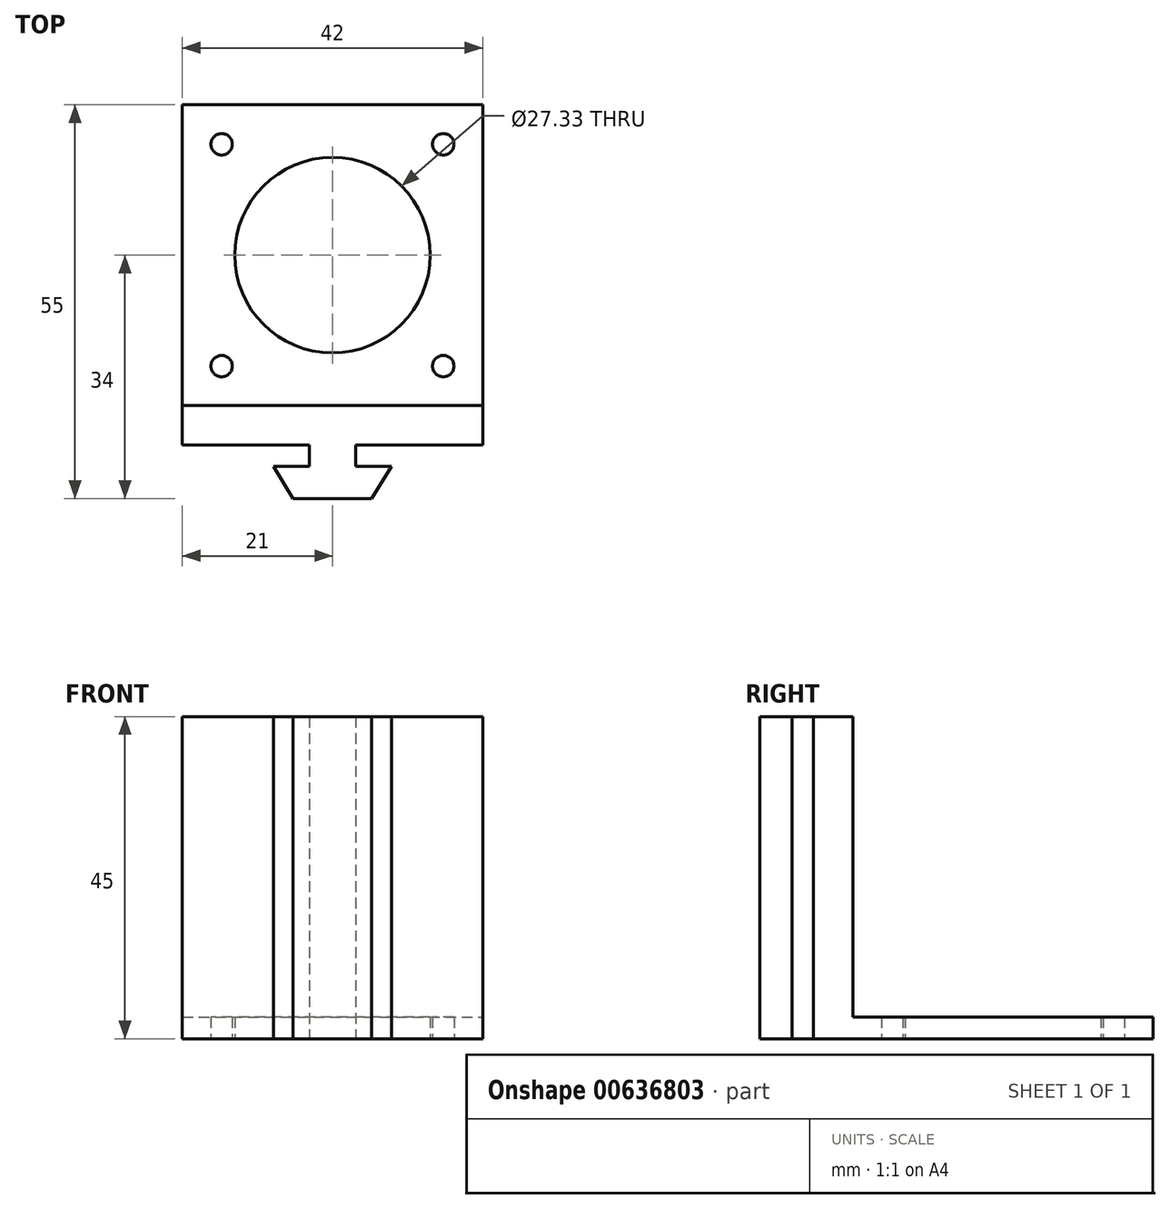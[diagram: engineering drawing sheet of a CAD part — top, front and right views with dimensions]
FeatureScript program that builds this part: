
annotation { "Feature Type Name" : "Feature", "Feature Type Description" : "" }
export const myFeature = defineFeature(function(context is Context, id is Id, definition is map)
    precondition{}
    {
        {
            var Q0;
            Q0=qCreatedBy(makeId("Top.planeOp"),FACE);
            var sketch = newSketch(context, id + "F0", { "sketchPlane" : qUnion([Q0])});
            skPoint(sketch, "E0.middle", {"position": v(0, 0) * mm});
            skLineSegment(sketch, "E1.bottom", {"start": v(-21, 21) * mm, "end": v(21, 21) * mm});
            skLineSegment(sketch, "E1.top", {"start": v(-21, -21) * mm, "end": v(21, -21) * mm});
            skLineSegment(sketch, "E1.left", {"start": v(-21, 21) * mm, "end": v(-21, -21) * mm});
            skLineSegment(sketch, "E1.right", {"start": v(21, 21) * mm, "end": v(21, -21) * mm});
            skLineSegment(sketch, "E2.bottom", {"start": v(15.5, -15.5) * mm, "end": v(-15.5, -15.5) * mm, "construction": true});
            skLineSegment(sketch, "E2.top", {"start": v(15.5, 15.5) * mm, "end": v(-15.5, 15.5) * mm, "construction": true});
            skLineSegment(sketch, "E2.left", {"start": v(15.5, -15.5) * mm, "end": v(15.5, 15.5) * mm, "construction": true});
            skLineSegment(sketch, "E2.right", {"start": v(-15.5, -15.5) * mm, "end": v(-15.5, 15.5) * mm, "construction": true});
            skCircle(sketch, "E3", {"center": v(-15.5, 15.5) * mm, "radius": 1.5 * mm});
            skCircle(sketch, "E4", {"center": v(15.5, 15.5) * mm, "radius": 1.5 * mm});
            skCircle(sketch, "E5", {"center": v(-15.5, -15.5) * mm, "radius": 1.5 * mm});
            skCircle(sketch, "E6", {"center": v(15.5, -15.5) * mm, "radius": 1.5 * mm});
            skLineSegment(sketch, "E7", {"start": v(0, -21) * mm, "end": v(3.25, -21) * mm});
            skLineSegment(sketch, "E8", {"start": v(3.25, -21) * mm, "end": v(3.25, -29.5) * mm});
            skLineSegment(sketch, "E9", {"start": v(3.25, -29.5) * mm, "end": v(8.25, -29.5) * mm});
            skLineSegment(sketch, "E10", {"start": v(0, -21) * mm, "end": v(0, -34) * mm});
            skLineSegment(sketch, "E11", {"start": v(0, -34) * mm, "end": v(5.5, -34) * mm});
            skLineSegment(sketch, "E12", {"start": v(5.5, -34) * mm, "end": v(8.25, -29.5) * mm});
            skLineSegment(sketch, "E13.MirrorCS", {"start": v(0, -34) * mm, "end": v(-5.5, -34) * mm});
            skLineSegment(sketch, "E14.MirrorCS", {"start": v(-5.5, -34) * mm, "end": v(-8.25, -29.5) * mm});
            skLineSegment(sketch, "E15.MirrorCS", {"start": v(-3.25, -29.5) * mm, "end": v(-8.25, -29.5) * mm});
            skLineSegment(sketch, "E16.MirrorCS", {"start": v(0, -21) * mm, "end": v(-3.25, -21) * mm});
            skLineSegment(sketch, "E17.MirrorCS", {"start": v(-3.25, -21) * mm, "end": v(-3.25, -26.5) * mm});
            skLineSegment(sketch, "E18.top", {"start": v(-21, -26.5) * mm, "end": v(21, -26.5) * mm});
            skLineSegment(sketch, "E18.left", {"start": v(-21, -21) * mm, "end": v(-21, -26.5) * mm});
            skLineSegment(sketch, "E18.right", {"start": v(21, -21) * mm, "end": v(21, -26.5) * mm});
            skCircle(sketch, "E19", {"center": v(0, 0) * mm, "radius": 13.67 * mm});
            skLineSegment(sketch, "E20", {"start": v(-3.25, -26.5) * mm, "end": v(-3.25, -29.5) * mm});
            skSolve(sketch);
        }
        {
            var Q0;
            Q0=makeQuery(id+"F0.imprint","IMPRINT",FACE,{"disambiguationData":[TD([[makeQuery(id+"F0.imprint","IMPRINT",EDGE,{"derivedFrom":sQuery(id+"F0.wireOp",EDGE,"E1.bottom")}),-1.0]])]});
            extrude(context, id + "F1", {"entities" : qUnion([Q0]), "depth" : 3 * mm, "offsetDistance" : 25 * mm});
        }
        {
            var Q0;
            {var subQ0=sQuery(id+"F0.wireOp",EDGE,"E13.MirrorCS");Q0=makeQuery(id+"F0.imprint","IMPRINT",FACE,{"disambiguationData":[TD([[makeQuery(id+"F0.imprint","IMPRINT",EDGE,{"derivedFrom":subQ0}),-1.0]])]});}
            var Q1;
            {var subQ4=sQuery(id+"F0.wireOp",EDGE,"E9");Q1=makeQuery(id+"F0.imprint","IMPRINT",FACE,{"disambiguationData":[TD([[makeQuery(id+"F0.imprint","IMPRINT",EDGE,{"derivedFrom":subQ4}),-1.0]])]});}
            var Q2;
            {var subQ0=sQuery(id+"F0.wireOp",EDGE,"E1.top");var subQ1=sQuery(id+"F0.wireOp",EDGE,"E8");var subQ2=makeQuery(id+"F0.imprint","INTERSECT",VERTEX,{"derivedFrom":[subQ1,subQ0]});Q2=makeQuery(id+"F0.imprint","IMPRINT",FACE,{"disambiguationData":[TD([[makeQuery(id+"F0.imprint","IMPRINT",EDGE,{"disambiguationData":[TD([[subQ2,-1.0]])],"derivedFrom":subQ1}),-1.0]])]});}
            var Q3;
            {var subQ5=sQuery(id+"F0.wireOp",EDGE,"E18.right");Q3=makeQuery(id+"F0.imprint","IMPRINT",FACE,{"disambiguationData":[TD([[makeQuery(id+"F0.imprint","IMPRINT",EDGE,{"derivedFrom":subQ5}),-1.0]])]});}
            var Q4;
            {var subQ0=sQuery(id+"F0.wireOp",EDGE,"E1.top");var subQ1=sQuery(id+"F0.wireOp",EDGE,"E10");var subQ2=makeQuery(id+"F0.imprint","INTERSECT",VERTEX,{"derivedFrom":[subQ1,subQ0]});Q4=makeQuery(id+"F0.imprint","IMPRINT",FACE,{"disambiguationData":[TD([[makeQuery(id+"F0.imprint","IMPRINT",EDGE,{"disambiguationData":[TD([[subQ2,-1.0]])],"derivedFrom":subQ1}),-1.0]])]});}
            var Q5;
            {var subQ5=sQuery(id+"F0.wireOp",EDGE,"E18.left");Q5=makeQuery(id+"F0.imprint","IMPRINT",FACE,{"disambiguationData":[TD([[makeQuery(id+"F0.imprint","IMPRINT",EDGE,{"derivedFrom":subQ5}),1.0]])]});}
            var Q6;
            {var subQ5=sQuery(id+"F0.wireOp",EDGE,"E11");Q6=makeQuery(id+"F0.imprint","IMPRINT",FACE,{"disambiguationData":[TD([[makeQuery(id+"F0.imprint","IMPRINT",EDGE,{"derivedFrom":subQ5}),1.0]])]});}
            extrude(context, id + "F2", {"entities" : qUnion([Q0, Q1, Q2, Q3, Q4, Q5, Q6]), "operationType" : NewBodyOperationType.ADD, "depth" : 45 * mm, "offsetDistance" : 25 * mm});
        }
    });
